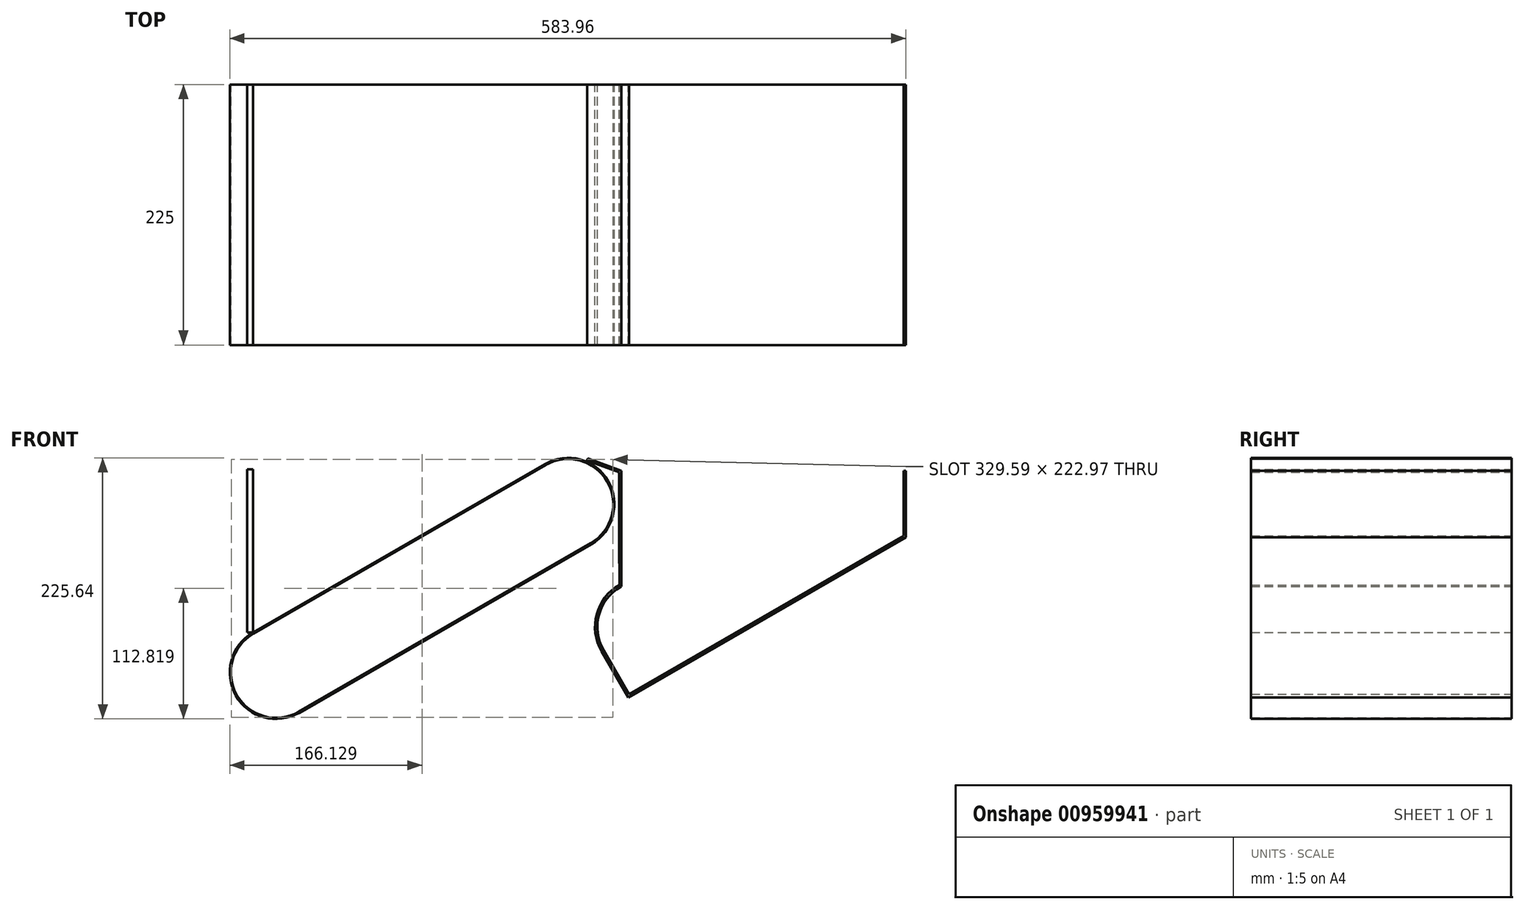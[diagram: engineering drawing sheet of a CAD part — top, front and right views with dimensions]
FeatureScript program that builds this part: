
annotation { "Feature Type Name" : "Feature", "Feature Type Description" : "" }
export const myFeature = defineFeature(function(context is Context, id is Id, definition is map)
    precondition{}
    {
        {
            var Q0;
            Q0=qCreatedBy(makeId("Front.planeOp"),FACE);
            var sketch = newSketch(context, id + "F0", { "sketchPlane" : qUnion([Q0])});
            skLineSegment(sketch, "E0", {"start": v(242.49, 0) * mm, "end": v(0, -140) * mm});
            skLineSegment(sketch, "E1", {"start": v(0, -140) * mm, "end": v(0, 0) * mm});
            skSolve(sketch);
        }
        {
            var Q0;
            Q0=qCreatedBy(makeId("Right.planeOp"),FACE);
            var sketch = newSketch(context, id + "F1", { "sketchPlane" : qUnion([Q0])});
            skLineSegment(sketch, "E2.bottom", {"start": v(-112.5, 0.5) * mm, "end": v(112.5, 0.5) * mm});
            skLineSegment(sketch, "E2.top", {"start": v(-112.5, -140.5) * mm, "end": v(112.5, -140.5) * mm});
            skLineSegment(sketch, "E2.left", {"start": v(-112.5, 0.5) * mm, "end": v(-112.5, -140.5) * mm});
            skLineSegment(sketch, "E2.right", {"start": v(112.5, 0.5) * mm, "end": v(112.5, -140.5) * mm});
            skPoint(sketch, "E2.middle", {"position": v(0, -70) * mm});
            skSolve(sketch);
        }
        {
            var Q0;
            Q0 = qSketchRegion(id + "F1", true);
            extrude(context, id + "F2", {"entities" : qUnion([Q0]), "oppositeDirection" : true, "depth" : 5 * mm, "offsetDistance" : 25 * mm});
        }
        {
            var Q0;
            Q0=qCreatedBy(makeId("Front.planeOp"),FACE);
            var sketch = newSketch(context, id + "F3", { "sketchPlane" : qUnion([Q0])});
            skLineSegment(sketch, "E3", {"start": v(272.26, -29.5) * mm, "end": v(20, -175.14) * mm});
            skArc(sketch, "E4.0.startCap", {"start": v(252.26, 5.14) * mm, "mid": v(306.9, -9.5) * mm, "end": v(292.26, -64.14) * mm});
            skArc(sketch, "E4.0.endCap", {"start": v(40, -209.78) * mm, "mid": v(-14.64, -195.14) * mm, "end": v(0, -140.5) * mm});
            skLineSegment(sketch, "E4.0.left", {"start": v(292.26, -64.14) * mm, "end": v(40, -209.78) * mm});
            skLineSegment(sketch, "E4.0.right", {"start": v(252.26, 5.14) * mm, "end": v(0, -140.5) * mm});
            skArc(sketch, "E5.0", {"start": v(252.76, 4.27) * mm, "mid": v(306.03, -10) * mm, "end": v(291.76, -63.27) * mm});
            skLineSegment(sketch, "E5.1", {"start": v(252.76, 4.27) * mm, "end": v(0.5, -141.37) * mm});
            skArc(sketch, "E5.2", {"start": v(39.5, -208.92) * mm, "mid": v(-13.77, -194.64) * mm, "end": v(0.5, -141.37) * mm});
            skLineSegment(sketch, "E5.3", {"start": v(291.76, -63.27) * mm, "end": v(39.5, -208.92) * mm});
            skSolve(sketch);
        }
        {
            var Q0;
            Q0 = qSketchRegion(id + "F3", true);
            extrude(context, id + "F4", {"entities" : qUnion([Q0]), "endBound" : BoundingType.SYMMETRIC, "depth" : 225 * mm, "offsetDistance" : 25 * mm});
        }
        {
            var Q0;
            Q0=qCreatedBy(makeId("Front.planeOp"),FACE);
            var sketch = newSketch(context, id + "F5", { "sketchPlane" : qUnion([Q0])});
            skLineSegment(sketch, "E6", {"start": v(290.08, 9.63) * mm, "end": v(318.27, -0.63) * mm});
            skPoint(sketch, "E7.visualSharp", {"position": v(296.56, 7.27) * mm});
            skArc(sketch, "E7.filletArc", {"start": v(290.08, 9.63) * mm, "mid": v(288.8, 9.03) * mm, "end": v(289.4, 7.75) * mm});
            skLineSegment(sketch, "E8", {"start": v(296.56, 7.27) * mm, "end": v(397.26, 7.27) * mm, "construction": true});
            skLineSegment(sketch, "E9", {"start": v(318.27, -0.63) * mm, "end": v(318.27, -100.63) * mm});
            skLineSegment(sketch, "E10", {"start": v(324.9, -193.8) * mm, "end": v(561.96, -56.93) * mm});
            skLineSegment(sketch, "E11", {"start": v(561.96, -56.93) * mm, "end": v(561.96, -0.63) * mm});
            skLineSegment(sketch, "E12.0", {"start": v(563.96, -58.09) * mm, "end": v(563.96, -0.63) * mm});
            skLineSegment(sketch, "E12.1", {"start": v(324.16, -196.53) * mm, "end": v(563.96, -58.09) * mm});
            skLineSegment(sketch, "E12.2", {"start": v(316.27, -2.03) * mm, "end": v(316.27, -62.59) * mm});
            skLineSegment(sketch, "E12.3", {"start": v(289.4, 7.75) * mm, "end": v(316.27, -2.03) * mm});
            skLineSegment(sketch, "E13", {"start": v(563.96, -0.63) * mm, "end": v(561.96, -0.63) * mm});
            skPoint(sketch, "E14.orphan", {"position": v(561.96, 0) * mm});
            skLineSegment(sketch, "E15", {"start": v(518.53, -31.2) * mm, "end": v(321.9, -144.72) * mm});
            skArc(sketch, "E16.0.startCap", {"start": v(498.53, 3.44) * mm, "mid": v(553.17, -11.2) * mm, "end": v(538.53, -65.84) * mm});
            skLineSegment(sketch, "E16.0.left", {"start": v(538.53, -65.84) * mm, "end": v(341.9, -179.37) * mm});
            skLineSegment(sketch, "E16.0.right", {"start": v(318.27, -100.63) * mm, "end": v(317.54, -101.05) * mm});
            skLineSegment(sketch, "E17", {"start": v(324.16, -196.53) * mm, "end": v(301.16, -156.7) * mm});
            skLineSegment(sketch, "E18", {"start": v(324.9, -193.8) * mm, "end": v(302.9, -155.7) * mm});
            skArc(sketch, "E19.trimOffspring", {"start": v(302.9, -155.7) * mm, "mid": v(298.9, -125.34) * mm, "end": v(317.54, -101.05) * mm});
            skArc(sketch, "E20.trimOffspring", {"start": v(301.16, -156.7) * mm, "mid": v(296.97, -124.83) * mm, "end": v(316.54, -99.32) * mm});
            skLineSegment(sketch, "E21.trimOffspring", {"start": v(316.27, -62.59) * mm, "end": v(316.54, -99.32) * mm});
            skSolve(sketch);
        }
        {
            var Q0;
            Q0 = qSketchRegion(id + "F5", true);
            extrude(context, id + "F6", {"entities" : qUnion([Q0]), "endBound" : BoundingType.SYMMETRIC, "depth" : 225 * mm, "offsetDistance" : 25 * mm});
        }
    });
